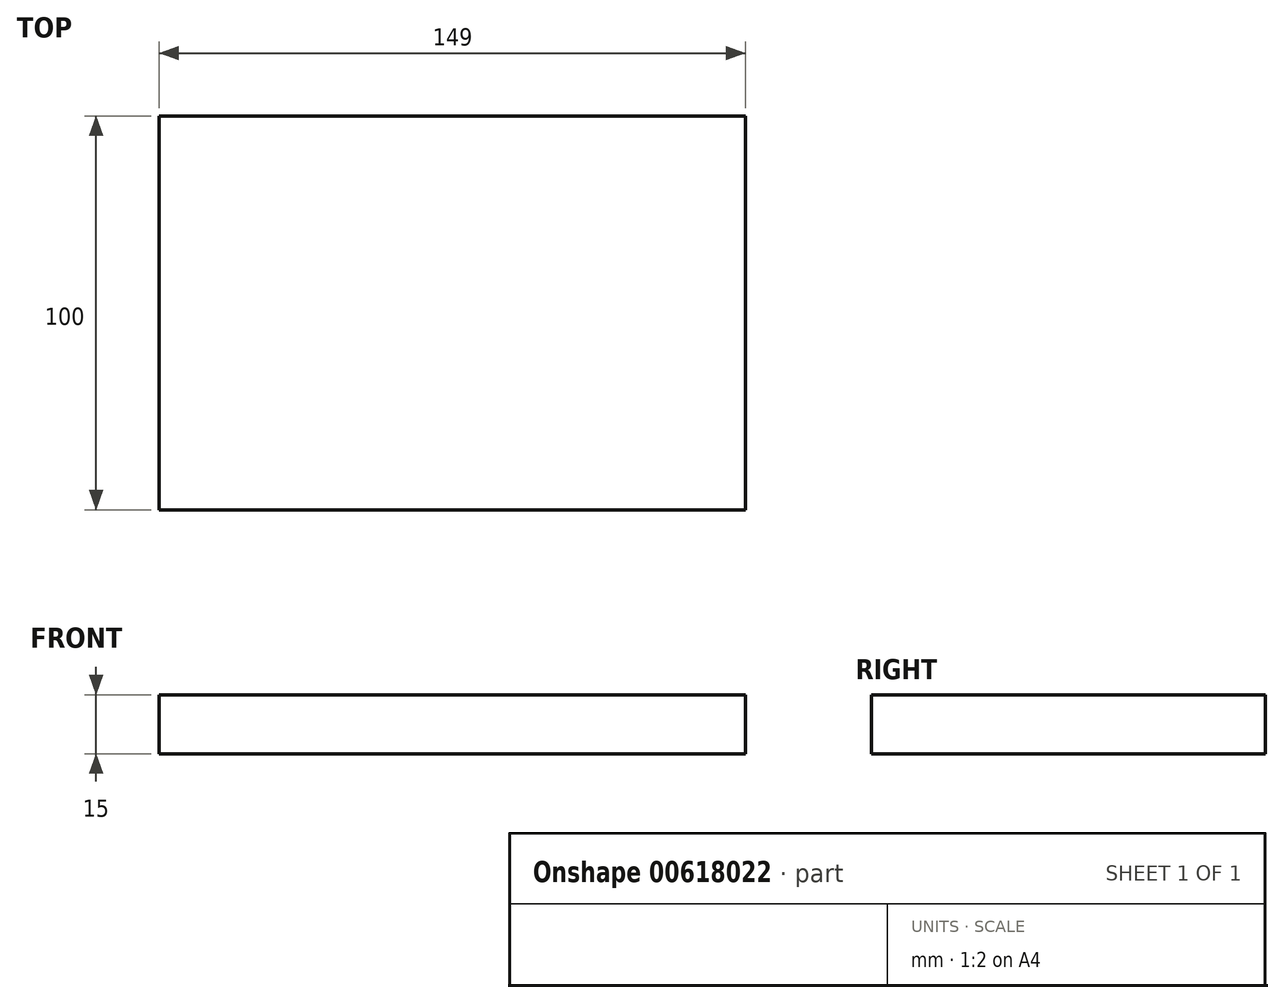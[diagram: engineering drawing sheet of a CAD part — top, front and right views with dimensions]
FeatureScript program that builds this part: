
annotation { "Feature Type Name" : "Feature", "Feature Type Description" : "" }
export const myFeature = defineFeature(function(context is Context, id is Id, definition is map)
    precondition{}
    {
        {
            var Q0;
            Q0=qCreatedBy(makeId("Top.planeOp"),FACE);
            var sketch = newSketch(context, id + "F0", { "sketchPlane" : qUnion([Q0])});
            skLineSegment(sketch, "E0.bottom", {"start": v(74.5, 50) * mm, "end": v(-74.5, 50) * mm});
            skLineSegment(sketch, "E0.top", {"start": v(74.5, -50) * mm, "end": v(-74.5, -50) * mm});
            skLineSegment(sketch, "E0.left", {"start": v(74.5, 50) * mm, "end": v(74.5, -50) * mm});
            skLineSegment(sketch, "E0.right", {"start": v(-74.5, 50) * mm, "end": v(-74.5, -50) * mm});
            skPoint(sketch, "E0.middle", {"position": v(0, 0) * mm});
            skSolve(sketch);
        }
        {
            var Q0;
            Q0=makeQuery(id+"F0.imprint","IMPRINT",FACE,{"disambiguationData":[TD([[makeQuery(id+"F0.imprint","IMPRINT",EDGE,{"derivedFrom":sQuery(id+"F0.wireOp",EDGE,"E0.bottom")}),1.0]])]});
            extrude(context, id + "F1", {"entities" : qUnion([Q0]), "depth" : 15 * mm, "offsetDistance" : 25 * mm});
        }
    });
